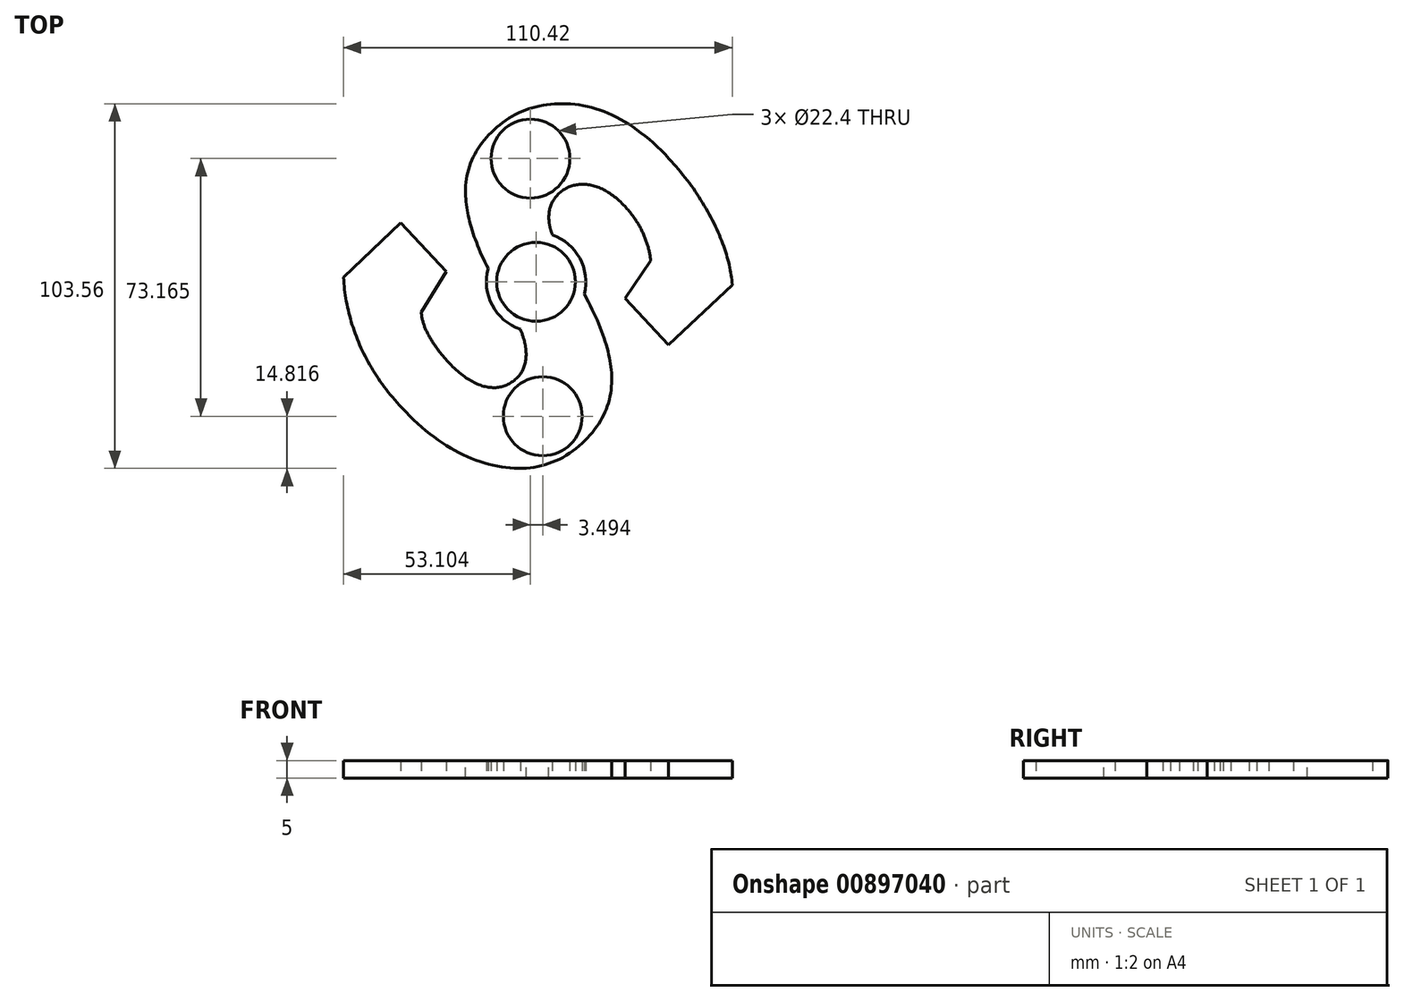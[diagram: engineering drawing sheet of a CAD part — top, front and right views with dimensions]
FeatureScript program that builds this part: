
annotation { "Feature Type Name" : "Feature", "Feature Type Description" : "" }
export const myFeature = defineFeature(function(context is Context, id is Id, definition is map)
    precondition{}
    {
        {
            var Q0;
            Q0=qCreatedBy(makeId("Top.planeOp"),FACE);
            var sketch = newSketch(context, id + "F0", { "sketchPlane" : qUnion([Q0])});
            skCircle(sketch, "E0", {"center": v(0, 0) * mm, "radius": 11.2 * mm});
            skText(sketch, "E1", { "text": "s", "fontName": "RobotoSlab-Bold.ttf"});
            skCircle(sketch, "E2", {"center": v(0, 0) * mm, "radius": 14.12 * mm});
            skPoint(sketch, "E3.center", {"position": v(-1.59, 35) * mm});
            skCircle(sketch, "E4", {"center": v(-1.59, 35) * mm, "radius": 11.2 * mm});
            skCircle(sketch, "E5", {"center": v(1.9, -38.16) * mm, "radius": 11.2 * mm});
            const initialGuessF0  = {"E1": [-0.07006, 0.00147, 0.68053, -0.73272, 0.13648]};
            skSetInitialGuess(sketch, initialGuessF0);
            skSolve(sketch);
        }
        {
            var Q0;
            Q0=makeQuery(id+"F0.imprint","IMPRINT",FACE,{"disambiguationData":[TD([[makeQuery(id+"F0.imprint","IMPRINT",EDGE,{"derivedFrom":sQuery(id+"F0.wireOp",EDGE,"E1.sketch_text.stroke-0")}),-1.0]])]});
            var Q1;
            {var subQ5=sQuery(id+"F0.wireOp",EDGE,"E1.sketch_text.stroke-7");var subQ6=sQuery(id+"F0.wireOp",EDGE,"E1.sketch_text.stroke-6");var subQ7=makeQuery(id+"F0.imprint","INTERSECT",VERTEX,{"derivedFrom":[subQ6,subQ5]});Q1=makeQuery(id+"F0.imprint","IMPRINT",FACE,{"disambiguationData":[TD([[makeQuery(id+"F0.imprint","IMPRINT",EDGE,{"disambiguationData":[TD([[subQ7,1.0]])],"derivedFrom":subQ6}),-1.0]])]});}
            var Q2;
            {var subQ7=sQuery(id+"F0.wireOp",EDGE,"E1.sketch_text.stroke-11");Q2=makeQuery(id+"F0.imprint","IMPRINT",FACE,{"disambiguationData":[TD([[makeQuery(id+"F0.imprint","IMPRINT",EDGE,{"derivedFrom":subQ7}),-1.0]])]});}
            var Q3;
            Q3=makeQuery(id+"F0.imprint","IMPRINT",FACE,{"disambiguationData":[TD([[makeQuery(id+"F0.imprint","IMPRINT",EDGE,{"derivedFrom":sQuery(id+"F0.wireOp",EDGE,"80f9ceac-4da1-4e9f-a352-9dbd9333a209")}),-1.0]])]});
            var Q4;
            {var subQ0=sQuery(id+"F0.wireOp",EDGE,"E1.sketch_text.stroke-8");var subQ1=sQuery(id+"F0.wireOp",EDGE,"E0");var subQ2=makeQuery(id+"F0.imprint","INTERSECT",VERTEX,{"derivedFrom":[subQ1,subQ0]});Q4=makeQuery(id+"F0.imprint","IMPRINT",FACE,{"disambiguationData":[TD([[makeQuery(id+"F0.imprint","IMPRINT",EDGE,{"disambiguationData":[TD([[subQ2,1.0]])],"derivedFrom":subQ1}),-1.0]])]});}
            var Q5;
            {var subQ0=sQuery(id+"F0.wireOp",EDGE,"E1.sketch_text.stroke-7");var subQ1=sQuery(id+"F0.wireOp",EDGE,"E0");var subQ2=makeQuery(id+"F0.imprint","INTERSECT",VERTEX,{"derivedFrom":[subQ1,subQ0]});Q5=makeQuery(id+"F0.imprint","IMPRINT",FACE,{"disambiguationData":[TD([[makeQuery(id+"F0.imprint","IMPRINT",EDGE,{"disambiguationData":[TD([[subQ2,-1.0]])],"derivedFrom":subQ1}),-1.0]])]});}
            var Q6;
            {var subQ0=sQuery(id+"F0.wireOp",EDGE,"E1.sketch_text.stroke-23");var subQ1=sQuery(id+"F0.wireOp",EDGE,"E0");var subQ2=makeQuery(id+"F0.imprint","INTERSECT",VERTEX,{"derivedFrom":[subQ1,subQ0]});Q6=makeQuery(id+"F0.imprint","IMPRINT",FACE,{"disambiguationData":[TD([[makeQuery(id+"F0.imprint","IMPRINT",EDGE,{"disambiguationData":[TD([[subQ2,-1.0]])],"derivedFrom":subQ1}),-1.0]])]});}
            var Q7;
            {var subQ0=sQuery(id+"F0.wireOp",EDGE,"E1.sketch_text.stroke-7");var subQ1=sQuery(id+"F0.wireOp",EDGE,"E0");var subQ2=makeQuery(id+"F0.imprint","INTERSECT",VERTEX,{"derivedFrom":[subQ1,subQ0]});Q7=makeQuery(id+"F0.imprint","IMPRINT",FACE,{"disambiguationData":[TD([[makeQuery(id+"F0.imprint","IMPRINT",EDGE,{"disambiguationData":[TD([[subQ2,1.0]])],"derivedFrom":subQ1}),-1.0]])]});}
            var Q8;
            {var subQ1=sQuery(id+"F0.wireOp",EDGE,"E1.sketch_text.stroke-10");var subQ6=sQuery(id+"F0.wireOp",EDGE,"E1.sketch_text.stroke-9");var subQ7=makeQuery(id+"F0.imprint","INTERSECT",VERTEX,{"derivedFrom":[subQ6,subQ1]});Q8=makeQuery(id+"F0.imprint","IMPRINT",FACE,{"disambiguationData":[TD([[makeQuery(id+"F0.imprint","IMPRINT",EDGE,{"disambiguationData":[TD([[subQ7,1.0]])],"derivedFrom":subQ6}),1.0]])]});}
            var Q9;
            {var subQ1=sQuery(id+"F0.wireOp",EDGE,"E1.sketch_text.stroke-10");var subQ6=sQuery(id+"F0.wireOp",EDGE,"E1.sketch_text.stroke-9");var subQ7=makeQuery(id+"F0.imprint","INTERSECT",VERTEX,{"derivedFrom":[subQ6,subQ1]});Q9=makeQuery(id+"F0.imprint","IMPRINT",FACE,{"disambiguationData":[TD([[makeQuery(id+"F0.imprint","IMPRINT",EDGE,{"disambiguationData":[TD([[subQ7,1.0]])],"derivedFrom":subQ6}),-1.0]])]});}
            extrude(context, id + "F1", {"entities" : qUnion([Q0, Q1, Q2, Q3, Q4, Q5, Q6, Q7, Q8, Q9]), "depth" : 5 * mm, "offsetDistance" : 25 * mm});
        }
    });
